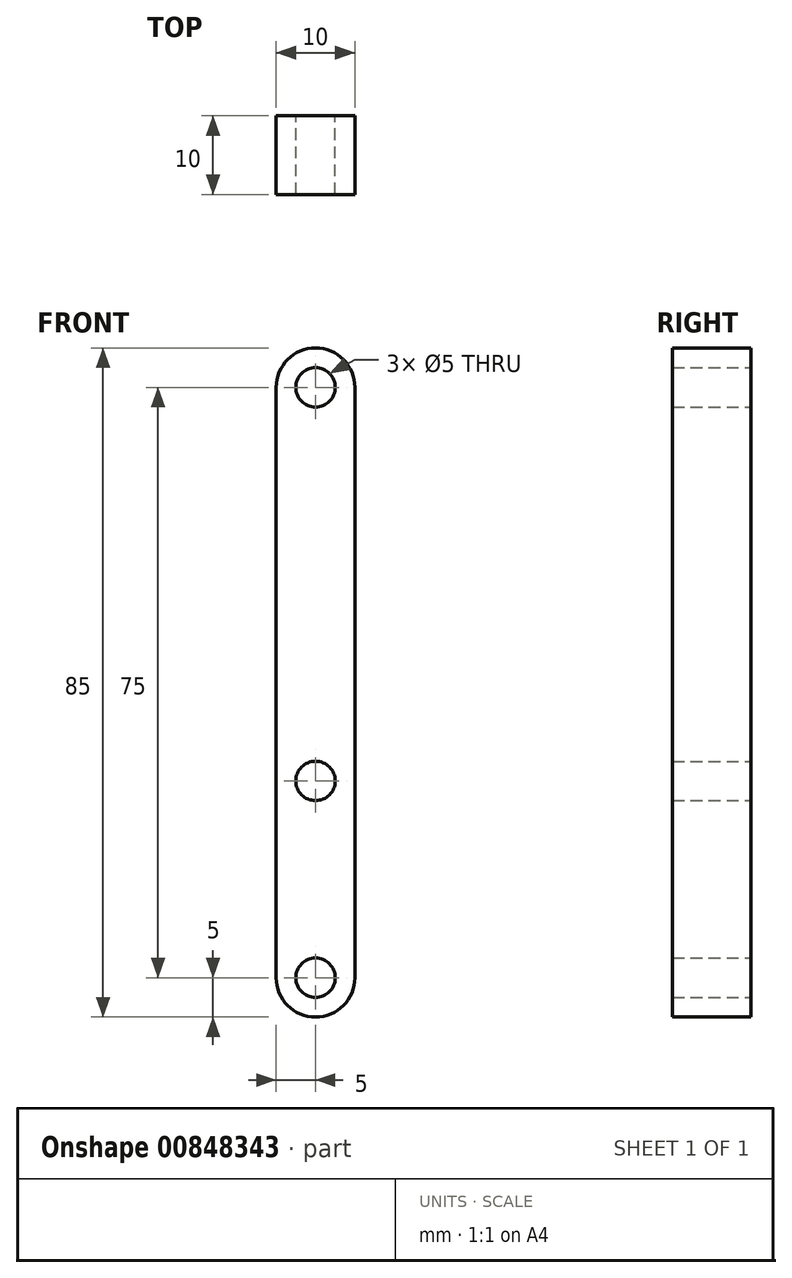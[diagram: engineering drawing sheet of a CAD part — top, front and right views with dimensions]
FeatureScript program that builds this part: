
annotation { "Feature Type Name" : "Feature", "Feature Type Description" : "" }
export const myFeature = defineFeature(function(context is Context, id is Id, definition is map)
    precondition{}
    {
        {
            var Q0;
            Q0=qCreatedBy(makeId("Front.planeOp"),FACE);
            var sketch = newSketch(context, id + "F0", { "sketchPlane" : qUnion([Q0])});
            skArc(sketch, "E0", {"start": v(5, 0) * mm, "mid": v(0, 5) * mm, "end": v(-5, 0) * mm});
            skArc(sketch, "E1", {"start": v(-5, -75) * mm, "mid": v(0, -80) * mm, "end": v(5, -75) * mm});
            skLineSegment(sketch, "E2", {"start": v(5, 0) * mm, "end": v(5, -75) * mm});
            skLineSegment(sketch, "E3", {"start": v(-5, 0) * mm, "end": v(-5, -75) * mm});
            skCircle(sketch, "E4", {"center": v(0, 0) * mm, "radius": 2.5 * mm});
            skCircle(sketch, "E5", {"center": v(0, -75) * mm, "radius": 2.5 * mm});
            skCircle(sketch, "E6", {"center": v(0, -50) * mm, "radius": 2.5 * mm});
            skLineSegment(sketch, "E7", {"start": v(0, 0) * mm, "end": v(0, 0) * mm});
            skLineSegment(sketch, "E8", {"start": v(0, 0) * mm, "end": v(6.63, 0) * mm, "construction": true});
            skSolve(sketch);
        }
        {
            var Q0;
            Q0=qSketchRegion(id+"F0",true);
            extrude(context, id + "F1", {"entities" : qUnion([Q0]), "depth" : 10 * mm, "offsetDistance" : 25 * mm});
        }
    });
